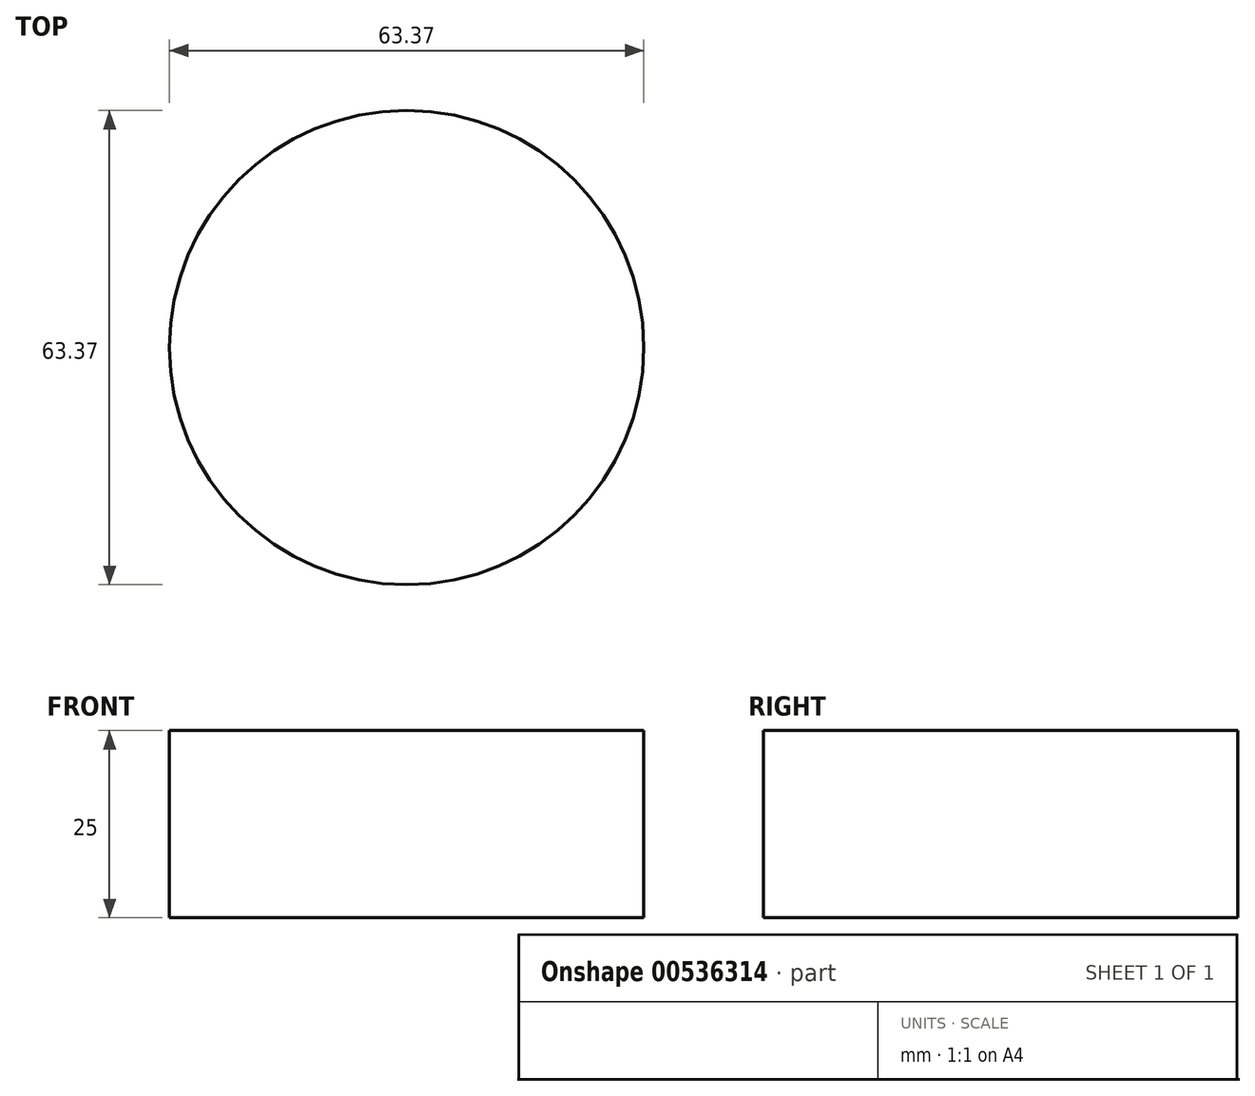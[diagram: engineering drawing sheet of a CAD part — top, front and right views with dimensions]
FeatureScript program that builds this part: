
annotation { "Feature Type Name" : "Feature", "Feature Type Description" : "" }
export const myFeature = defineFeature(function(context is Context, id is Id, definition is map)
    precondition{}
    {
        {
            var Q0;
            Q0=qCreatedBy(makeId("Top.planeOp"),FACE);
            var sketch = newSketch(context, id + "F0", { "sketchPlane" : qUnion([Q0])});
            skLineSegment(sketch, "E0.bottom", {"start": v(0, 0) * mm, "end": v(89, 0) * mm});
            skLineSegment(sketch, "E0.top", {"start": v(0, 100) * mm, "end": v(89, 100) * mm});
            skLineSegment(sketch, "E0.left", {"start": v(0, 0) * mm, "end": v(0, 100) * mm});
            skLineSegment(sketch, "E0.right", {"start": v(89, 0) * mm, "end": v(89, 100) * mm});
            skSolve(sketch);
        }
        {
            var Q0;
            Q0=makeQuery(id+"F0.imprint","IMPRINT",FACE,{"disambiguationData":[TD([[makeQuery(id+"F0.imprint","IMPRINT",EDGE,{"derivedFrom":sQuery(id+"F0.wireOp",EDGE,"E0.bottom")}),1.0]])]});
            extrude(context, id + "F1", {"entities" : qUnion([Q0]), "depth" : 25 * mm, "offsetDistance" : 25 * mm});
        }
        {
            var Q0;
            Q0=makeQuery(id+"F1.opExtrude","CAP_FACE",FACE,{"disambiguationData":[OSD([sQuery(id+"F0.wireOp",EDGE,"E0.bottom"),sQuery(id+"F0.wireOp",EDGE,"E0.top"),sQuery(id+"F0.wireOp",EDGE,"E0.left"),sQuery(id+"F0.wireOp",EDGE,"E0.right")])],"isStart":false});
            var sketch = newSketch(context, id + "F2", { "sketchPlane" : qUnion([Q0])});
            skCircle(sketch, "E1", {"center": v(44.42, 52.56) * mm, "radius": 31.69 * mm});
            skSolve(sketch);
        }
        {
            var Q0;
            Q0=makeQuery(id+"F2.imprint","IMPRINT",FACE,{"disambiguationData":[TD([[makeQuery(id+"F2.imprint","IMPRINT",EDGE,{"derivedFrom":sQuery(id+"F2.wireOp",EDGE,"E1")}),1.0]])]});
            extrude(context, id + "F3", {"entities" : qUnion([Q0]), "operationType" : NewBodyOperationType.INTERSECT, "oppositeDirection" : true, "depth" : 25 * mm, "offsetDistance" : 25 * mm});
        }
    });
